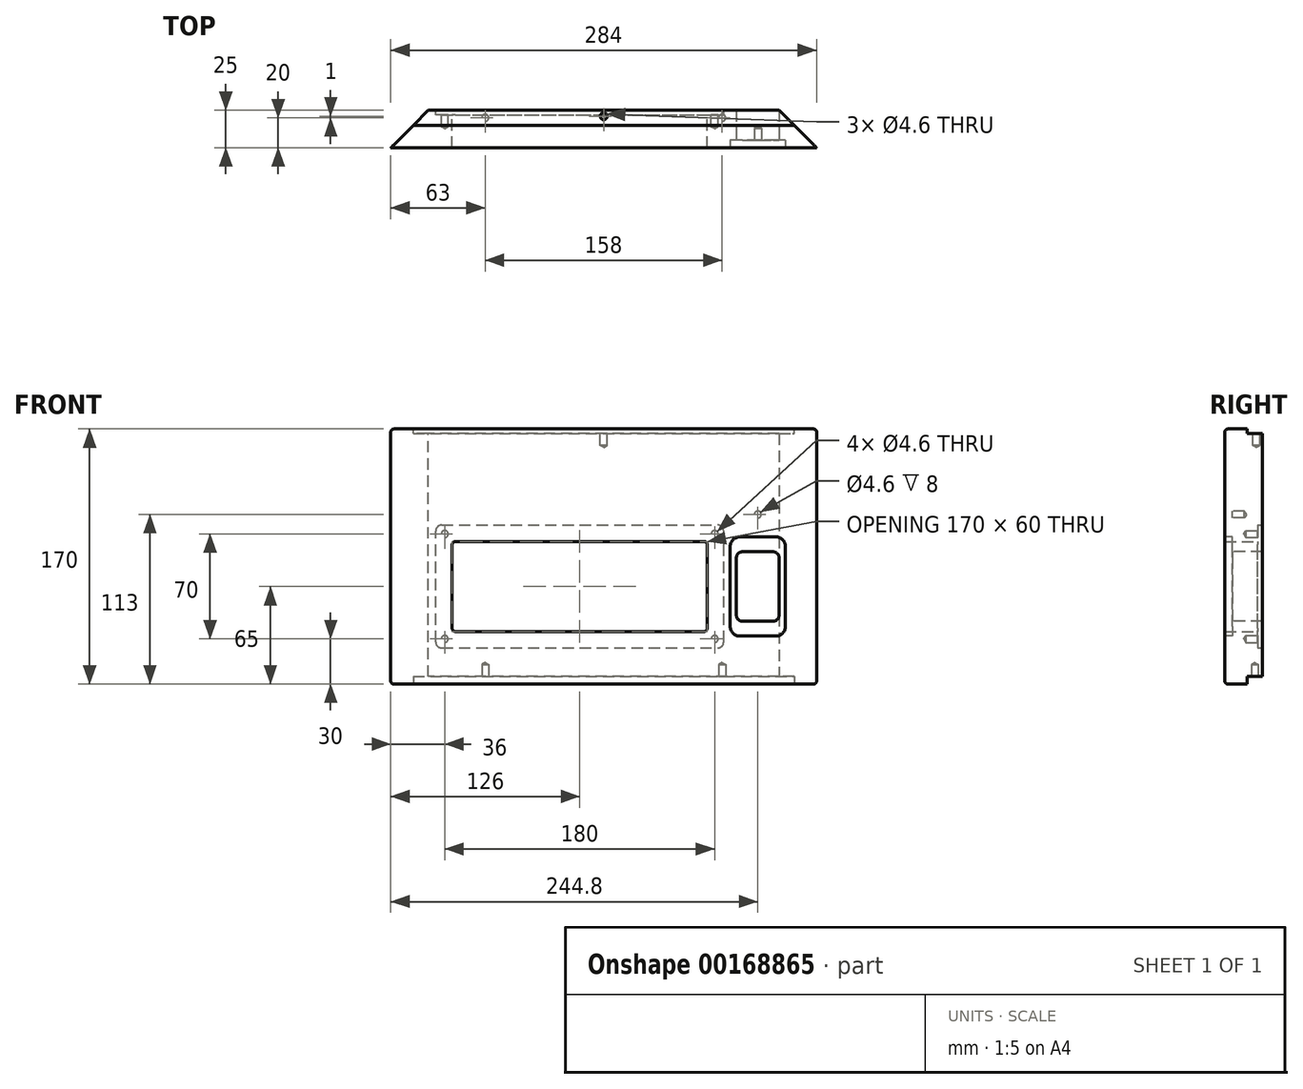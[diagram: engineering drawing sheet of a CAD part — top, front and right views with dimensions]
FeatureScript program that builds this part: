
annotation { "Feature Type Name" : "Feature", "Feature Type Description" : "" }
export const myFeature = defineFeature(function(context is Context, id is Id, definition is map)
    precondition{}
    {
        {
            var Q0;
            Q0=qCreatedBy(makeId("Front.planeOp"),FACE);
            var sketch = newSketch(context, id + "F0", { "sketchPlane" : qUnion([Q0])});
            skLineSegment(sketch, "E0.bottom", {"start": v(142, -85) * mm, "end": v(-142, -85) * mm});
            skLineSegment(sketch, "E0.top", {"start": v(142, 85) * mm, "end": v(-142, 85) * mm});
            skLineSegment(sketch, "E0.left", {"start": v(142, -85) * mm, "end": v(142, 85) * mm});
            skLineSegment(sketch, "E0.right", {"start": v(-142, -85) * mm, "end": v(-142, 85) * mm});
            skPoint(sketch, "E0.middle", {"position": v(0, 0) * mm});
            skSolve(sketch);
        }
        {
            var Q0;
            Q0=makeQuery(id+"F0.imprint","IMPRINT",FACE,{"disambiguationData":[TD([[makeQuery(id+"F0.imprint","IMPRINT",EDGE,{"derivedFrom":sQuery(id+"F0.wireOp",EDGE,"E0.bottom")}),-1.0]])]});
            extrude(context, id + "F1", {"entities" : qUnion([Q0]), "depth" : 25 * mm});
        }
        {
            var Q0;
            Q0=makeQuery(id+"F1.opExtrude","CAP_EDGE",EDGE,{"disambiguationData":[OSD([sQuery(id+"F0.wireOp",EDGE,"E0.right")])],"isStart":true});
            var Q1;
            Q1=makeQuery(id+"F1.opExtrude","CAP_EDGE",EDGE,{"disambiguationData":[OSD([sQuery(id+"F0.wireOp",EDGE,"E0.left")])],"isStart":true});
            chamfer(context, id + "F2", {"entities" : qUnion([Q0, Q1]), "width" : 25 * mm, "tangentPropagation" : true});
        }
        {
            var Q0;
            Q0=makeQuery(id+"F1.opExtrude","SWEPT_FACE",FACE,{"disambiguationData":[OSD([sQuery(id+"F0.wireOp",EDGE,"E0.top")])]});
            var sketch = newSketch(context, id + "F3", { "sketchPlane" : qUnion([Q0])});
            skLineSegment(sketch, "E1", {"start": v(-127, -10) * mm, "end": v(127, -10) * mm});
            skSolve(sketch);
        }
        {
            var Q0;
            {var subQ0=sQuery(id+"F3.wireOp",EDGE,"E1");Q0=makeQuery(id+"F3.imprint","IMPRINT",FACE,{"disambiguationData":[TD([[makeQuery(id+"F3.imprint","IMPRINT",EDGE,{"derivedFrom":subQ0}),1.0]])]});}
            extrude(context, id + "F4", {"entities" : qUnion([Q0]), "operationType" : NewBodyOperationType.REMOVE, "oppositeDirection" : true, "depth" : 3 * mm});
        }
        {
            var Q0;
            Q0=makeQuery(id+"F1.opExtrude","SWEPT_FACE",FACE,{"disambiguationData":[OSD([sQuery(id+"F0.wireOp",EDGE,"E0.bottom")])]});
            var sketch = newSketch(context, id + "F5", { "sketchPlane" : qUnion([Q0])});
            skLineSegment(sketch, "E2", {"start": v(-127, 10) * mm, "end": v(127, 10) * mm});
            skSolve(sketch);
        }
        {
            var Q0;
            {var subQ0=sQuery(id+"F5.wireOp",EDGE,"E2");Q0=makeQuery(id+"F5.imprint","IMPRINT",FACE,{"disambiguationData":[TD([[makeQuery(id+"F5.imprint","IMPRINT",EDGE,{"derivedFrom":subQ0}),-1.0]])]});}
            extrude(context, id + "F6", {"entities" : qUnion([Q0]), "operationType" : NewBodyOperationType.REMOVE, "oppositeDirection" : true, "depth" : 5 * mm});
        }
        {
            var Q0;
            Q0=makeQuery(id+"F1.opExtrude","CAP_FACE",FACE,{"disambiguationData":[OSD([sQuery(id+"F0.wireOp",EDGE,"E0.bottom"),sQuery(id+"F0.wireOp",EDGE,"E0.top"),sQuery(id+"F0.wireOp",EDGE,"E0.left"),sQuery(id+"F0.wireOp",EDGE,"E0.right")])],"isStart":false});
            var sketch = newSketch(context, id + "F7", { "sketchPlane" : qUnion([Q0])});
            skLineSegment(sketch, "E3.bottom", {"start": v(92.5, 3.15) * mm, "end": v(113, 3.15) * mm});
            skLineSegment(sketch, "E3.top", {"start": v(92.5, -43.15) * mm, "end": v(113, -43.15) * mm});
            skLineSegment(sketch, "E3.left", {"start": v(88.5, -0.85) * mm, "end": v(88.5, -39.15) * mm});
            skLineSegment(sketch, "E3.right", {"start": v(117, -0.85) * mm, "end": v(117, -39.15) * mm});
            skLineSegment(sketch, "E4", {"start": v(0, -20) * mm, "end": v(92, -20) * mm, "construction": true});
            skPoint(sketch, "E5.visualSharp", {"position": v(117, 3.15) * mm});
            skArc(sketch, "E5.filletArc", {"start": v(117, -0.85) * mm, "mid": v(115.83, 1.98) * mm, "end": v(113, 3.15) * mm});
            skPoint(sketch, "E6.visualSharp", {"position": v(88.5, 3.15) * mm});
            skArc(sketch, "E6.filletArc", {"start": v(92.5, 3.15) * mm, "mid": v(89.67, 1.98) * mm, "end": v(88.5, -0.85) * mm});
            skPoint(sketch, "E7.visualSharp", {"position": v(88.5, -43.15) * mm});
            skArc(sketch, "E7.filletArc", {"start": v(88.5, -39.15) * mm, "mid": v(89.67, -41.98) * mm, "end": v(92.5, -43.15) * mm});
            skPoint(sketch, "E8.visualSharp", {"position": v(117, -43.15) * mm});
            skArc(sketch, "E8.filletArc", {"start": v(113, -43.15) * mm, "mid": v(115.83, -41.98) * mm, "end": v(117, -39.15) * mm});
            skLineSegment(sketch, "E9.bottom", {"start": v(114.7, -53.1) * mm, "end": v(90.9, -53.1) * mm});
            skLineSegment(sketch, "E9.top", {"start": v(114.7, 13.1) * mm, "end": v(90.9, 13.1) * mm});
            skLineSegment(sketch, "E9.left", {"start": v(121.2, -46.6) * mm, "end": v(121.2, 6.6) * mm});
            skLineSegment(sketch, "E9.right", {"start": v(84.4, -46.6) * mm, "end": v(84.4, 6.6) * mm});
            skPoint(sketch, "E9.middle", {"position": v(102.8, -20) * mm});
            skPoint(sketch, "E10.visualSharp", {"position": v(84.4, 13.1) * mm});
            skArc(sketch, "E10.filletArc", {"start": v(90.9, 13.1) * mm, "mid": v(86.3, 11.2) * mm, "end": v(84.4, 6.6) * mm});
            skPoint(sketch, "E11.visualSharp", {"position": v(121.2, 13.1) * mm});
            skArc(sketch, "E11.filletArc", {"start": v(121.2, 6.6) * mm, "mid": v(119.3, 11.2) * mm, "end": v(114.7, 13.1) * mm});
            skPoint(sketch, "E12.visualSharp", {"position": v(121.2, -53.1) * mm});
            skArc(sketch, "E12.filletArc", {"start": v(114.7, -53.1) * mm, "mid": v(119.3, -51.2) * mm, "end": v(121.2, -46.6) * mm});
            skPoint(sketch, "E13.visualSharp", {"position": v(84.4, -53.1) * mm});
            skArc(sketch, "E13.filletArc", {"start": v(84.4, -46.6) * mm, "mid": v(86.3, -51.2) * mm, "end": v(90.9, -53.1) * mm});
            skSolve(sketch);
        }
        {
            var Q0;
            Q0=makeQuery(id+"F7.imprint","IMPRINT",FACE,{"disambiguationData":[TD([[makeQuery(id+"F7.imprint","IMPRINT",EDGE,{"derivedFrom":sQuery(id+"F7.wireOp",EDGE,"E3.bottom")}),-1.0]])]});
            extrude(context, id + "F8", {"entities" : qUnion([Q0]), "operationType" : NewBodyOperationType.REMOVE, "endBound" : BoundingType.THROUGH_ALL, "oppositeDirection" : true, "depth" : 25 * mm});
        }
        {
            var Q0;
            Q0=makeQuery(id+"F0.imprint","IMPRINT",FACE,{"disambiguationData":[TD([[makeQuery(id+"F0.imprint","IMPRINT",EDGE,{"derivedFrom":sQuery(id+"F0.wireOp",EDGE,"E0.bottom")}),-1.0]])]});
            var sketch = newSketch(context, id + "F9", { "sketchPlane" : qUnion([Q0])});
            skLineSegment(sketch, "E14.bottom", {"start": v(-108, -61) * mm, "end": v(76, -61) * mm});
            skLineSegment(sketch, "E14.top", {"start": v(-108, 21) * mm, "end": v(76, 21) * mm});
            skLineSegment(sketch, "E14.left", {"start": v(-112, -57) * mm, "end": v(-112, 17) * mm});
            skLineSegment(sketch, "E14.right", {"start": v(80, -57) * mm, "end": v(80, 17) * mm});
            skPoint(sketch, "E14.middle", {"position": v(-16, -20) * mm});
            skPoint(sketch, "E15.visualSharp", {"position": v(80, 21) * mm});
            skArc(sketch, "E15.filletArc", {"start": v(80, 17) * mm, "mid": v(78.83, 19.83) * mm, "end": v(76, 21) * mm});
            skPoint(sketch, "E16.visualSharp", {"position": v(-112, 21) * mm});
            skArc(sketch, "E16.filletArc", {"start": v(-108, 21) * mm, "mid": v(-110.83, 19.83) * mm, "end": v(-112, 17) * mm});
            skPoint(sketch, "E17.visualSharp", {"position": v(-112, -61) * mm});
            skArc(sketch, "E17.filletArc", {"start": v(-112, -57) * mm, "mid": v(-110.83, -59.83) * mm, "end": v(-108, -61) * mm});
            skPoint(sketch, "E18.visualSharp", {"position": v(80, -61) * mm});
            skArc(sketch, "E18.filletArc", {"start": v(76, -61) * mm, "mid": v(78.83, -59.83) * mm, "end": v(80, -57) * mm});
            skLineSegment(sketch, "E19.bottom", {"start": v(-99, -50) * mm, "end": v(67, -50) * mm});
            skLineSegment(sketch, "E19.top", {"start": v(-99, 10) * mm, "end": v(67, 10) * mm});
            skLineSegment(sketch, "E19.left", {"start": v(-101, -48) * mm, "end": v(-101, 8) * mm});
            skLineSegment(sketch, "E19.right", {"start": v(69, -48) * mm, "end": v(69, 8) * mm});
            skPoint(sketch, "E20.visualSharp", {"position": v(69, 10) * mm});
            skArc(sketch, "E20.filletArc", {"start": v(69, 8) * mm, "mid": v(68.41, 9.41) * mm, "end": v(67, 10) * mm});
            skPoint(sketch, "E21.visualSharp", {"position": v(-101, 10) * mm});
            skArc(sketch, "E21.filletArc", {"start": v(-99, 10) * mm, "mid": v(-100.41, 9.41) * mm, "end": v(-101, 8) * mm});
            skPoint(sketch, "E22.visualSharp", {"position": v(-101, -50) * mm});
            skArc(sketch, "E22.filletArc", {"start": v(-101, -48) * mm, "mid": v(-100.41, -49.41) * mm, "end": v(-99, -50) * mm});
            skPoint(sketch, "E23.visualSharp", {"position": v(69, -50) * mm});
            skArc(sketch, "E23.filletArc", {"start": v(67, -50) * mm, "mid": v(68.41, -49.41) * mm, "end": v(69, -48) * mm});
            skSolve(sketch);
        }
        {
            var Q0;
            Q0 = qSketchRegion(id + "F9", true);
            extrude(context, id + "F10", {"entities" : qUnion([Q0]), "operationType" : NewBodyOperationType.REMOVE, "depth" : 3 * mm});
        }
        {
            var Q0;
            Q0=makeQuery(id+"F7.imprint","IMPRINT",FACE,{"disambiguationData":[TD([[makeQuery(id+"F7.imprint","IMPRINT",EDGE,{"derivedFrom":sQuery(id+"F7.wireOp",EDGE,"E3.bottom")}),1.0]])]});
            extrude(context, id + "F11", {"entities" : qUnion([Q0]), "operationType" : NewBodyOperationType.REMOVE, "oppositeDirection" : true, "depth" : 5.1 * mm});
        }
        {
            var Q0;
            Q0=makeQuery(id+"F11.boolean.opBoolean","COPY",FACE,{"derivedFrom":makeQuery(id+"F11.opExtrude","CAP_FACE",FACE,{"disambiguationData":[OSD([sQuery(id+"F7.wireOp",EDGE,"E3.bottom"),sQuery(id+"F7.wireOp",EDGE,"E3.top"),sQuery(id+"F7.wireOp",EDGE,"E3.left"),sQuery(id+"F7.wireOp",EDGE,"E3.right"),sQuery(id+"F7.wireOp",EDGE,"E5.filletArc"),sQuery(id+"F7.wireOp",EDGE,"E6.filletArc"),sQuery(id+"F7.wireOp",EDGE,"E7.filletArc"),sQuery(id+"F7.wireOp",EDGE,"E8.filletArc"),sQuery(id+"F7.wireOp",EDGE,"E9.bottom"),sQuery(id+"F7.wireOp",EDGE,"E9.top"),sQuery(id+"F7.wireOp",EDGE,"E9.left"),sQuery(id+"F7.wireOp",EDGE,"E9.right"),sQuery(id+"F7.wireOp",EDGE,"E10.filletArc"),sQuery(id+"F7.wireOp",EDGE,"E11.filletArc"),sQuery(id+"F7.wireOp",EDGE,"E12.filletArc"),sQuery(id+"F7.wireOp",EDGE,"E13.filletArc")])],"isStart":false})});
            var sketch = newSketch(context, id + "F12", { "sketchPlane" : qUnion([Q0])});
            skLineSegment(sketch, "E24", {"start": v(102.8, 36.2) * mm, "end": v(102.8, 16.23) * mm, "construction": true});
            skLineSegment(sketch, "E25", {"start": v(79.7, 28) * mm, "end": v(125.49, 28) * mm, "construction": true});
            skLineSegment(sketch, "E26", {"start": v(81.27, -28) * mm, "end": v(123.54, -28) * mm, "construction": true});
            skLineSegment(sketch, "E27", {"start": v(102.8, -21.46) * mm, "end": v(102.8, -30.65) * mm, "construction": true});
            skPoint(sketch, "E28", {"position": v(102.8, 28) * mm});
            skPoint(sketch, "E29", {"position": v(102.8, -28) * mm});
            skSolve(sketch);
        }
        {
            var Q0;
            Q0=sQuery(id+"F12.wireOp",VERTEX,"E28");
            var Q1;
            Q1=sQuery(id+"F12.wireOp",VERTEX,"E29");
            var Q2;
            Q2=makeQuery(id+"F1.opExtrude","SWEPT_BODY",BODY,{"disambiguationData":[OSD([sQuery(id+"F0.wireOp",EDGE,"E0.bottom"),sQuery(id+"F0.wireOp",EDGE,"E0.top"),sQuery(id+"F0.wireOp",EDGE,"E0.left"),sQuery(id+"F0.wireOp",EDGE,"E0.right")])]});
            hole(context, id + "F13", {"style" : HoleStyle.SIMPLE, "endStyle" : HoleEndStyle.BLIND, "holeDiameter" : 4.6 * mm, "holeDepth" : 8 * mm, "startFromSketch" : true, "locations" : qUnion([Q0, Q1]), "scope" : qUnion([Q2])});
        }
        {
            var Q0;
            Q0=makeQuery(id+"F10.boolean.opBoolean","SPLIT",FACE,{"disambiguationData":[TD([makeQuery(id+"F10.opExtrude","SWEPT_FACE",FACE,{"disambiguationData":[OSD([sQuery(id+"F9.wireOp",EDGE,"E19.bottom")])]})])],"derivedFrom":makeQuery(id+"F1.opExtrude","CAP_FACE",FACE,{"disambiguationData":[OSD([sQuery(id+"F0.wireOp",EDGE,"E0.bottom"),sQuery(id+"F0.wireOp",EDGE,"E0.top"),sQuery(id+"F0.wireOp",EDGE,"E0.left"),sQuery(id+"F0.wireOp",EDGE,"E0.right")])],"isStart":true})});
            extrude(context, id + "F14", {"entities" : qUnion([Q0]), "operationType" : NewBodyOperationType.REMOVE, "endBound" : BoundingType.THROUGH_ALL, "oppositeDirection" : true, "depth" : 25 * mm});
        }
        {
            var Q0;
            Q0=makeQuery(id+"F10.boolean.opBoolean","COPY",FACE,{"derivedFrom":makeQuery(id+"F10.opExtrude","CAP_FACE",FACE,{"disambiguationData":[OSD([sQuery(id+"F9.wireOp",EDGE,"E14.bottom"),sQuery(id+"F9.wireOp",EDGE,"E14.top"),sQuery(id+"F9.wireOp",EDGE,"E14.left"),sQuery(id+"F9.wireOp",EDGE,"E14.right"),sQuery(id+"F9.wireOp",EDGE,"E15.filletArc"),sQuery(id+"F9.wireOp",EDGE,"E16.filletArc"),sQuery(id+"F9.wireOp",EDGE,"E17.filletArc"),sQuery(id+"F9.wireOp",EDGE,"E18.filletArc"),sQuery(id+"F9.wireOp",EDGE,"E19.bottom"),sQuery(id+"F9.wireOp",EDGE,"E19.top"),sQuery(id+"F9.wireOp",EDGE,"E19.left"),sQuery(id+"F9.wireOp",EDGE,"E19.right"),sQuery(id+"F9.wireOp",EDGE,"E20.filletArc"),sQuery(id+"F9.wireOp",EDGE,"E21.filletArc"),sQuery(id+"F9.wireOp",EDGE,"E22.filletArc"),sQuery(id+"F9.wireOp",EDGE,"E23.filletArc")])],"isStart":false})});
            var sketch = newSketch(context, id + "F15", { "sketchPlane" : qUnion([Q0])});
            skLineSegment(sketch, "E30", {"start": v(-74, 45.92) * mm, "end": v(-74, -54.76) * mm, "construction": true});
            skLineSegment(sketch, "E31", {"start": v(106, 50.84) * mm, "end": v(106, -52.8) * mm, "construction": true});
            skLineSegment(sketch, "E32", {"start": v(-88.36, 15) * mm, "end": v(119.3, 15) * mm, "construction": true});
            skLineSegment(sketch, "E33", {"start": v(-86.86, -55) * mm, "end": v(123.65, -55) * mm, "construction": true});
            skPoint(sketch, "E34", {"position": v(-74, 15) * mm});
            skPoint(sketch, "E35", {"position": v(106, 15) * mm});
            skPoint(sketch, "E36", {"position": v(106, -55) * mm});
            skPoint(sketch, "E37", {"position": v(-74, -55) * mm});
            skSolve(sketch);
        }
        {
            var Q0;
            Q0=sQuery(id+"F15.wireOp",VERTEX,"E34");
            var Q1;
            Q1=sQuery(id+"F15.wireOp",VERTEX,"E35");
            var Q2;
            Q2=sQuery(id+"F15.wireOp",VERTEX,"E36");
            var Q3;
            Q3=sQuery(id+"F15.wireOp",VERTEX,"E37");
            var Q4;
            Q4=makeQuery(id+"F1.opExtrude","SWEPT_BODY",BODY,{"disambiguationData":[OSD([sQuery(id+"F0.wireOp",EDGE,"E0.bottom"),sQuery(id+"F0.wireOp",EDGE,"E0.top"),sQuery(id+"F0.wireOp",EDGE,"E0.left"),sQuery(id+"F0.wireOp",EDGE,"E0.right")])]});
            hole(context, id + "F16", {"style" : HoleStyle.SIMPLE, "endStyle" : HoleEndStyle.BLIND, "holeDiameter" : 4.6 * mm, "holeDepth" : 8 * mm, "startFromSketch" : true, "locations" : qUnion([Q0, Q1, Q2, Q3]), "scope" : qUnion([Q4])});
        }
        {
            var Q0;
            Q0=makeQuery(id+"F4.boolean.opBoolean","COPY",FACE,{"derivedFrom":makeQuery(id+"F4.opExtrude","CAP_FACE",FACE,{"disambiguationData":[OSD([sQuery(id+"F0.wireOp",EDGE,"E0.top"),sQuery(id+"F0.wireOp",EDGE,"E0.left"),sQuery(id+"F0.wireOp",EDGE,"E0.right"),sQuery(id+"F3.wireOp",EDGE,"E1")])],"isStart":false})});
            var sketch = newSketch(context, id + "F17", { "sketchPlane" : qUnion([Q0])});
            skLineSegment(sketch, "E38", {"start": v(-125.51, -4) * mm, "end": v(119.08, -4) * mm, "construction": true});
            skLineSegment(sketch, "E39", {"start": v(0, 6.88) * mm, "end": v(0, -25.49) * mm, "construction": true});
            skPoint(sketch, "E39.endSnap0", {"position": v(0, -10) * mm});
            skPoint(sketch, "E40", {"position": v(0, -4) * mm});
            skSolve(sketch);
        }
        {
            var Q0;
            Q0=sQuery(id+"F17.wireOp",VERTEX,"E40");
            var Q1;
            Q1=makeQuery(id+"F1.opExtrude","SWEPT_BODY",BODY,{"disambiguationData":[OSD([sQuery(id+"F0.wireOp",EDGE,"E0.bottom"),sQuery(id+"F0.wireOp",EDGE,"E0.top"),sQuery(id+"F0.wireOp",EDGE,"E0.left"),sQuery(id+"F0.wireOp",EDGE,"E0.right")])]});
            hole(context, id + "F18", {"style" : HoleStyle.SIMPLE, "endStyle" : HoleEndStyle.BLIND, "holeDiameter" : 4.6 * mm, "holeDepth" : 8 * mm, "startFromSketch" : true, "locations" : qUnion([Q0]), "scope" : qUnion([Q1])});
        }
        {
            var Q0;
            Q0=makeQuery(id+"F6.boolean.opBoolean","COPY",FACE,{"derivedFrom":makeQuery(id+"F6.opExtrude","CAP_FACE",FACE,{"disambiguationData":[OSD([sQuery(id+"F0.wireOp",EDGE,"E0.bottom"),sQuery(id+"F0.wireOp",EDGE,"E0.left"),sQuery(id+"F0.wireOp",EDGE,"E0.right"),sQuery(id+"F5.wireOp",EDGE,"E2")])],"isStart":false})});
            var sketch = newSketch(context, id + "F19", { "sketchPlane" : qUnion([Q0])});
            skLineSegment(sketch, "E41", {"start": v(-139.49, 5) * mm, "end": v(132.14, 5) * mm, "construction": true});
            skPoint(sketch, "E41.endSnap0", {"position": v(122, 5) * mm});
            skLineSegment(sketch, "E42", {"start": v(-79, 19.2) * mm, "end": v(-79, -13.88) * mm, "construction": true});
            skLineSegment(sketch, "E43", {"start": v(0, 25.09) * mm, "end": v(0, -14.6) * mm, "construction": true});
            skLineSegment(sketch, "E44", {"start": v(79, 23.98) * mm, "end": v(79, -15.34) * mm, "construction": true});
            skPoint(sketch, "E45", {"position": v(-79, 5) * mm});
            skPoint(sketch, "E46", {"position": v(0, 5) * mm});
            skPoint(sketch, "E47", {"position": v(79, 5) * mm});
            skSolve(sketch);
        }
        {
            var Q0;
            Q0=sQuery(id+"F19.wireOp",VERTEX,"E45");
            var Q1;
            Q1=sQuery(id+"F19.wireOp",VERTEX,"E47");
            var Q2;
            Q2=makeQuery(id+"F1.opExtrude","SWEPT_BODY",BODY,{"disambiguationData":[OSD([sQuery(id+"F0.wireOp",EDGE,"E0.bottom"),sQuery(id+"F0.wireOp",EDGE,"E0.top"),sQuery(id+"F0.wireOp",EDGE,"E0.left"),sQuery(id+"F0.wireOp",EDGE,"E0.right")])]});
            hole(context, id + "F20", {"style" : HoleStyle.SIMPLE, "endStyle" : HoleEndStyle.BLIND, "holeDiameter" : 4.6 * mm, "holeDepth" : 8 * mm, "startFromSketch" : true, "locations" : qUnion([Q0, Q1]), "scope" : qUnion([Q2])});
        }
        {
            var Q0;
            Q0=makeQuery(id+"F1.opExtrude","CAP_EDGE",EDGE,{"disambiguationData":[OSD([sQuery(id+"F0.wireOp",EDGE,"E0.top")])],"isStart":false});
            var Q1;
            Q1=makeQuery(id+"F1.opExtrude","CAP_EDGE",EDGE,{"disambiguationData":[OSD([sQuery(id+"F0.wireOp",EDGE,"E0.bottom")])],"isStart":false});
            fillet(context, id + "F21", {"entities" : qUnion([Q0, Q1]), "radius" : 2 * mm, "tangentPropagation" : true, "allowEdgeOverflow" : false});
        }
    });
